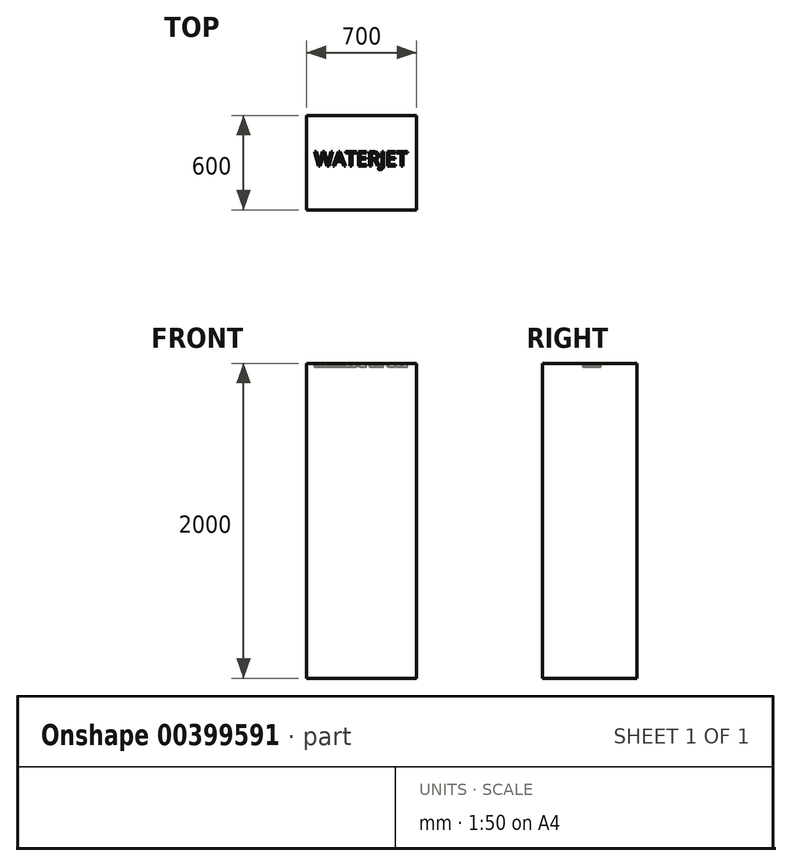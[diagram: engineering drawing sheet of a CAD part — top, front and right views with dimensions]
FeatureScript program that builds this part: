
annotation { "Feature Type Name" : "Feature", "Feature Type Description" : "" }
export const myFeature = defineFeature(function(context is Context, id is Id, definition is map)
    precondition{}
    {
        {
            var Q0;
            Q0=qCreatedBy(makeId("Top.planeOp"),FACE);
            var sketch = newSketch(context, id + "F0", { "sketchPlane" : qUnion([Q0])});
            skLineSegment(sketch, "E0.bottom", {"start": v(350, -300) * mm, "end": v(-350, -300) * mm});
            skLineSegment(sketch, "E0.top", {"start": v(350, 300) * mm, "end": v(-350, 300) * mm});
            skLineSegment(sketch, "E0.left", {"start": v(350, -300) * mm, "end": v(350, 300) * mm});
            skLineSegment(sketch, "E0.right", {"start": v(-350, -300) * mm, "end": v(-350, 300) * mm});
            skPoint(sketch, "E0.middle", {"position": v(0, 0) * mm});
            skSolve(sketch);
        }
        {
            var Q0;
            Q0 = qSketchRegion(id + "F0", true);
            extrude(context, id + "F1", {"entities" : qUnion([Q0]), "depth" : 2000 * mm});
        }
        {
            var Q0;
            Q0=makeQuery(id+"F1.opExtrude","CAP_FACE",FACE,{"disambiguationData":[OSD([sQuery(id+"F0.wireOp",EDGE,"E0.bottom"),sQuery(id+"F0.wireOp",EDGE,"E0.top"),sQuery(id+"F0.wireOp",EDGE,"E0.left"),sQuery(id+"F0.wireOp",EDGE,"E0.right")])],"isStart":false});
            var sketch = newSketch(context, id + "F2", { "sketchPlane" : qUnion([Q0])});
            skText(sketch, "E1", { "text": "WATERJET\n", "fontName": "OpenSans-Regular.ttf"});
            const initialGuessF2  = {"E1": [-0.3, -0.02154, 1, 0, 0.09137]};
            skSetInitialGuess(sketch, initialGuessF2);
            skSolve(sketch);
        }
        {
            var Q0;
            Q0 = qSketchRegion(id + "F2", true);
            extrude(context, id + "F3", {"entities" : qUnion([Q0]), "operationType" : NewBodyOperationType.REMOVE, "oppositeDirection" : true, "depth" : 25 * mm});
        }
    });
